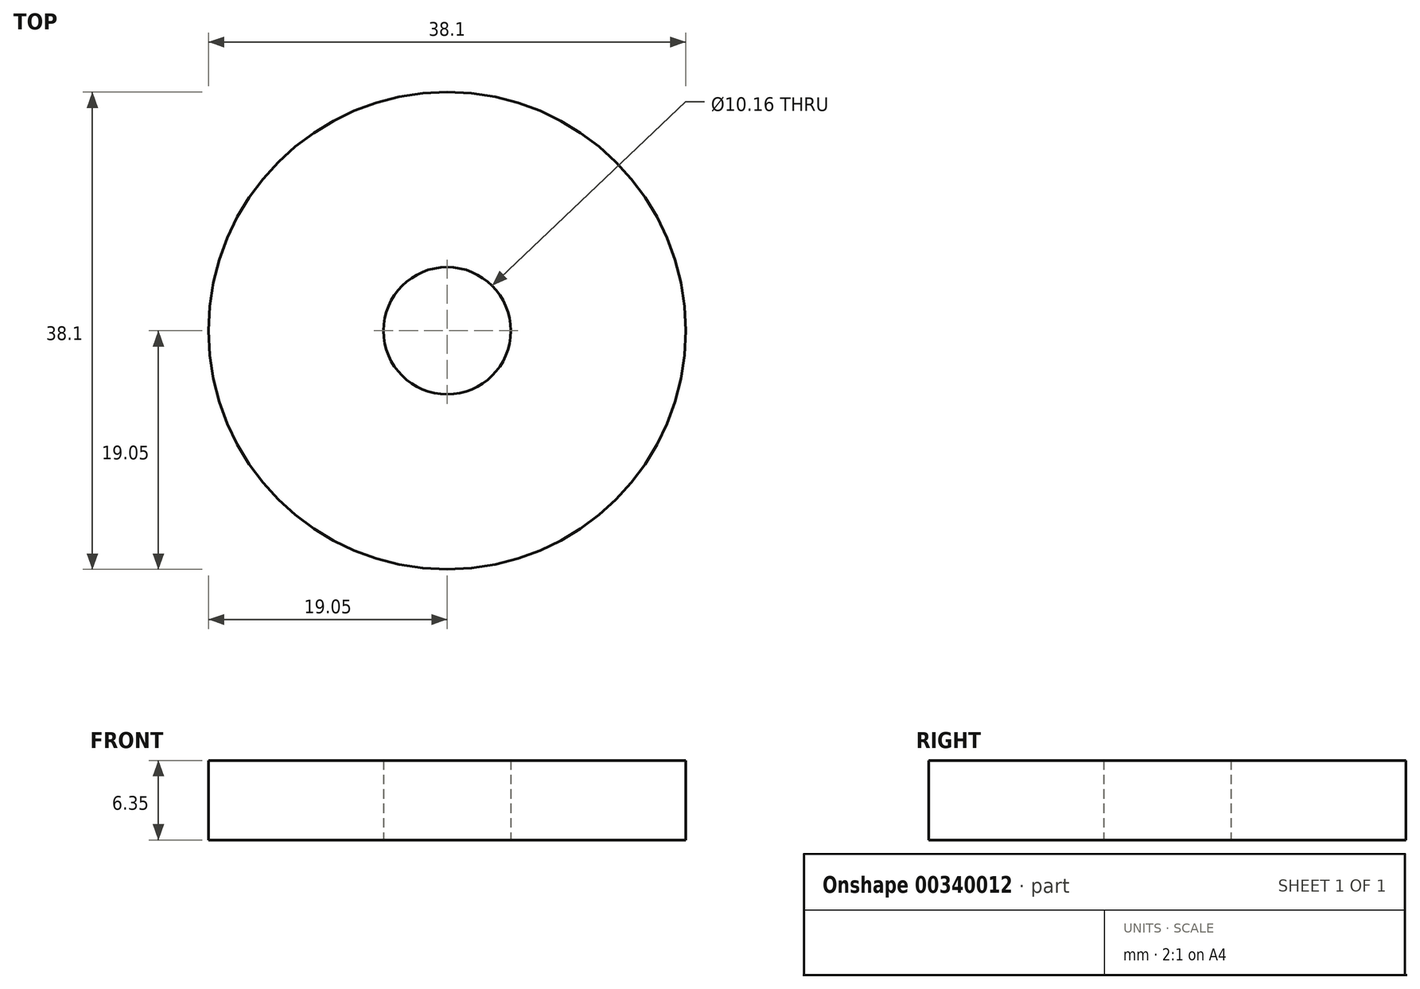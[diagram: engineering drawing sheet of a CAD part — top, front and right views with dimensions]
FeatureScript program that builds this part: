
annotation { "Feature Type Name" : "Feature", "Feature Type Description" : "" }
export const myFeature = defineFeature(function(context is Context, id is Id, definition is map)
    precondition{}
    {
        {
            var Q0;
            Q0=qCreatedBy(makeId("Top.planeOp"),FACE);
            var sketch = newSketch(context, id + "F0", { "sketchPlane" : qUnion([Q0])});
            skCircle(sketch, "E0", {"center": v(0, 0) * mm, "radius": 19.05 * mm});
            skCircle(sketch, "E1", {"center": v(0, 0) * mm, "radius": 5.08 * mm});
            skSolve(sketch);
        }
        {
            var Q0;
            Q0 = qSketchRegion(id + "F0", true);
            extrude(context, id + "F1", {"entities" : qUnion([Q0]), "depth" : 6.35 * mm});
        }
    });
